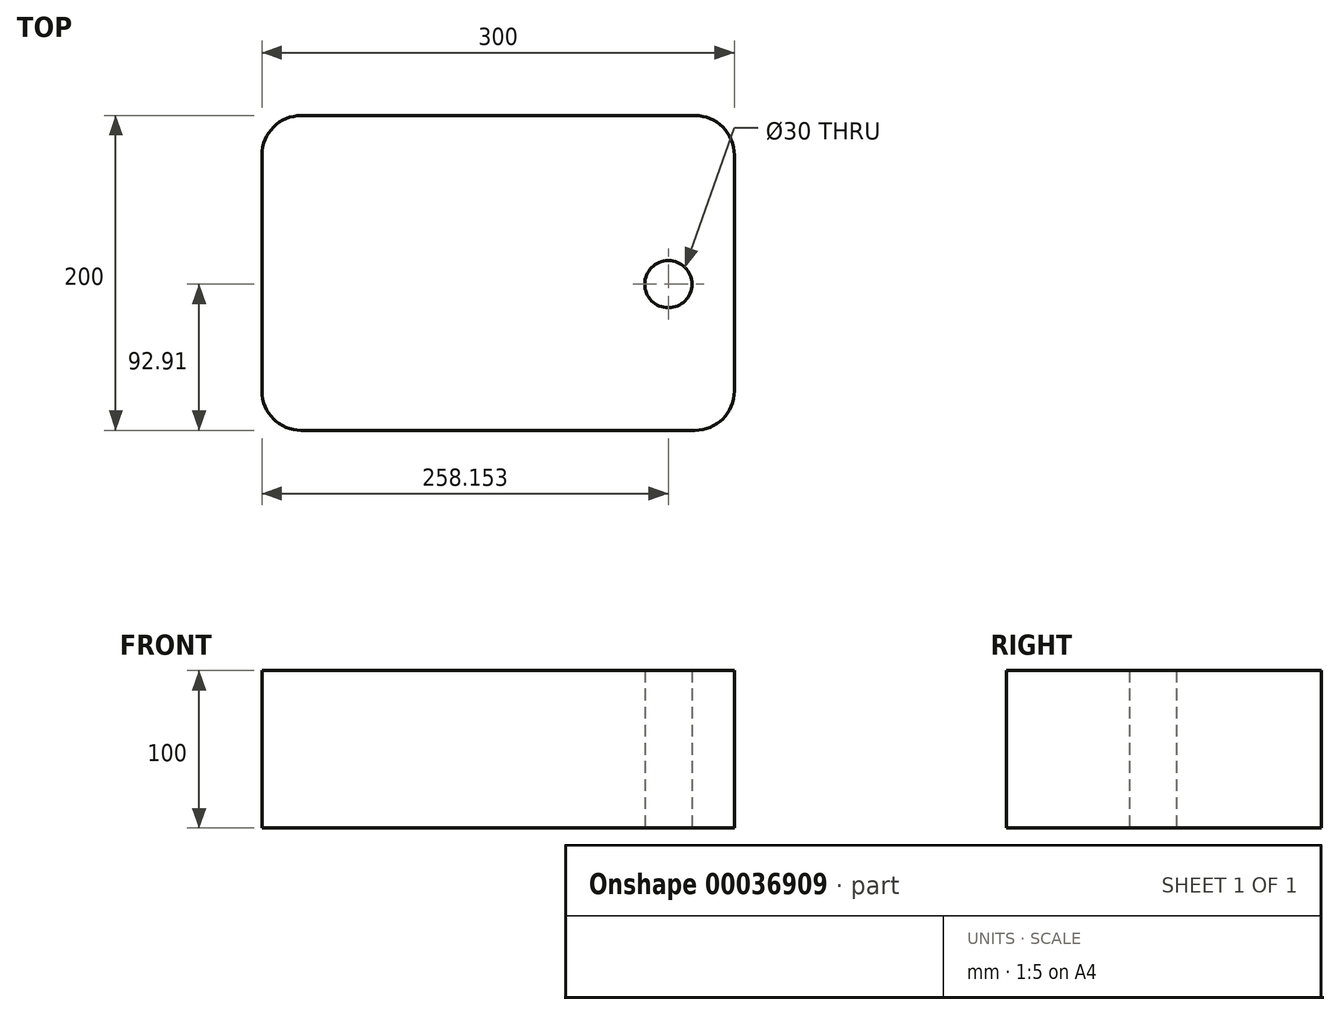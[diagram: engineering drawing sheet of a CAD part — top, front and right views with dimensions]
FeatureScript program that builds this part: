
annotation { "Feature Type Name" : "Feature", "Feature Type Description" : "" }
export const myFeature = defineFeature(function(context is Context, id is Id, definition is map)
    precondition{}
    {
        {
            var Q0;
            Q0=qCreatedBy(makeId("Top.planeOp"),FACE);
            var sketch = newSketch(context, id + "F0", { "sketchPlane" : qUnion([Q0])});
            skLineSegment(sketch, "E0.bottom", {"start": v(-142.76, 107.09) * mm, "end": v(157.24, 107.09) * mm});
            skLineSegment(sketch, "E0.top", {"start": v(-142.76, -92.91) * mm, "end": v(157.24, -92.91) * mm});
            skLineSegment(sketch, "E0.left", {"start": v(-142.76, 107.09) * mm, "end": v(-142.76, -92.91) * mm});
            skLineSegment(sketch, "E0.right", {"start": v(157.24, 107.09) * mm, "end": v(157.24, -92.91) * mm});
            skCircle(sketch, "E1", {"center": v(115.4, 0) * mm, "radius": 15 * mm});
            skSolve(sketch);
        }
        {
            var Q0;
            Q0=makeQuery(id+"F0.imprint","IMPRINT",FACE,{"disambiguationData":[TD([[makeQuery(id+"F0.imprint","IMPRINT",EDGE,{"derivedFrom":sQuery(id+"F0.wireOp",EDGE,"E0.bottom")}),-1.0]])]});
            extrude(context, id + "F1", {"entities" : qUnion([Q0]), "depth" : 100 * mm});
        }
        {
            var Q0;
            Q0=makeQuery(id+"F1.opExtrude","SWEPT_EDGE",EDGE,{"disambiguationData":[OSD([sQuery(id+"F0.wireOp",EDGE,"E0.bottom"),sQuery(id+"F0.wireOp",EDGE,"E0.right")])]});
            fillet(context, id + "F2", {"entities" : qUnion([Q0]), "radius" : 25 * mm, "tangentPropagation" : true, "allowEdgeOverflow" : false});
        }
        {
            var Q0;
            Q0=makeQuery(id+"F1.opExtrude","SWEPT_EDGE",EDGE,{"disambiguationData":[OSD([sQuery(id+"F0.wireOp",EDGE,"E0.bottom"),sQuery(id+"F0.wireOp",EDGE,"E0.left")])]});
            var Q1;
            Q1=makeQuery(id+"F1.opExtrude","SWEPT_EDGE",EDGE,{"disambiguationData":[OSD([sQuery(id+"F0.wireOp",EDGE,"E0.top"),sQuery(id+"F0.wireOp",EDGE,"E0.left")])]});
            var Q2;
            Q2=makeQuery(id+"F1.opExtrude","SWEPT_EDGE",EDGE,{"disambiguationData":[OSD([sQuery(id+"F0.wireOp",EDGE,"E0.top"),sQuery(id+"F0.wireOp",EDGE,"E0.right")])]});
            fillet(context, id + "F3", {"entities" : qUnion([Q0, Q1, Q2]), "radius" : 25 * mm, "tangentPropagation" : true, "allowEdgeOverflow" : false});
        }
    });
